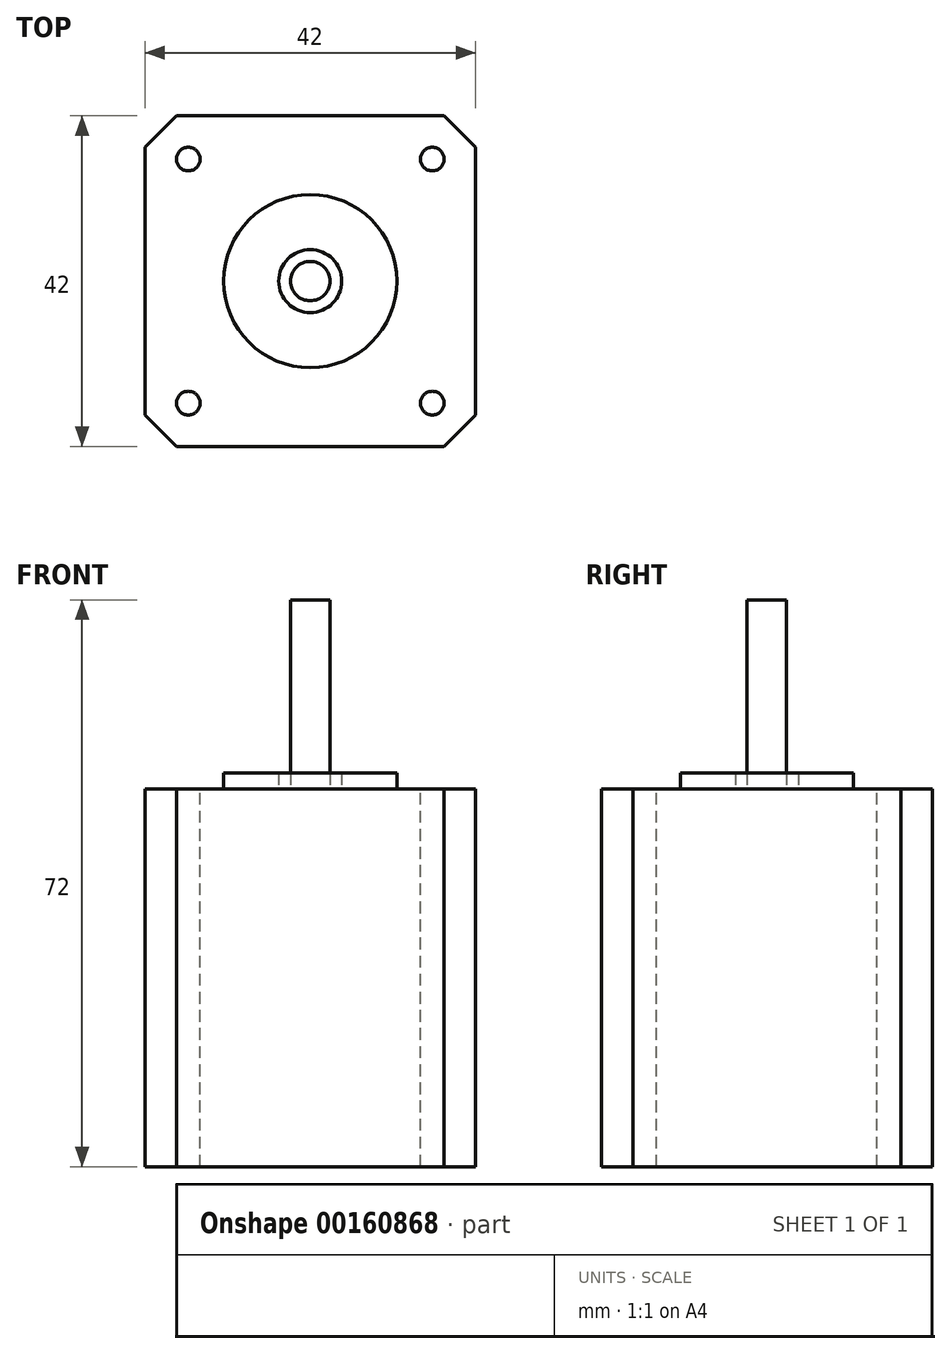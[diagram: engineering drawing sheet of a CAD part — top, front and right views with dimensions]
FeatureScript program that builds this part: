
annotation { "Feature Type Name" : "Feature", "Feature Type Description" : "" }
export const myFeature = defineFeature(function(context is Context, id is Id, definition is map)
    precondition{}
    {
        {
            var Q0;
            Q0=qCreatedBy(makeId("Top.planeOp"),FACE);
            var sketch = newSketch(context, id + "F0", { "sketchPlane" : qUnion([Q0])});
            skLineSegment(sketch, "E0", {"start": v(-21, 0) * mm, "end": v(-21, 17) * mm});
            skLineSegment(sketch, "E1", {"start": v(-21, 17) * mm, "end": v(-17, 21) * mm});
            skLineSegment(sketch, "E2", {"start": v(-17, 21) * mm, "end": v(0, 21) * mm});
            skLineSegment(sketch, "E3.MirrorCS", {"start": v(17, 21) * mm, "end": v(0, 21) * mm});
            skLineSegment(sketch, "E4.MirrorCS", {"start": v(21, 17) * mm, "end": v(17, 21) * mm});
            skLineSegment(sketch, "E5.MirrorCS", {"start": v(21, 0) * mm, "end": v(21, 17) * mm});
            skLineSegment(sketch, "E6.MirrorCS", {"start": v(21, 0) * mm, "end": v(21, -17) * mm});
            skLineSegment(sketch, "E7.MirrorCS", {"start": v(21, -17) * mm, "end": v(17, -21) * mm});
            skLineSegment(sketch, "E8.MirrorCS", {"start": v(17, -21) * mm, "end": v(0, -21) * mm});
            skLineSegment(sketch, "E9.MirrorCS", {"start": v(-17, -21) * mm, "end": v(0, -21) * mm});
            skLineSegment(sketch, "E10.MirrorCS", {"start": v(-21, -17) * mm, "end": v(-17, -21) * mm});
            skLineSegment(sketch, "E11.MirrorCS", {"start": v(-21, 0) * mm, "end": v(-21, -17) * mm});
            skCircle(sketch, "E12", {"center": v(15.5, 15.5) * mm, "radius": 1.5 * mm});
            skCircle(sketch, "E13.MirrorC", {"center": v(-15.5, 15.5) * mm, "radius": 1.5 * mm});
            skCircle(sketch, "E14.MirrorC", {"center": v(15.5, -15.5) * mm, "radius": 1.5 * mm});
            skCircle(sketch, "E15.MirrorC", {"center": v(-15.5, -15.5) * mm, "radius": 1.5 * mm});
            skSolve(sketch);
        }
        {
            var Q0;
            Q0 = qSketchRegion(id + "F0", true);
            extrude(context, id + "F1", {"entities" : qUnion([Q0]), "oppositeDirection" : true, "depth" : 48 * mm});
        }
        {
            var Q0;
            Q0=makeQuery(id+"F1.opExtrude","CAP_FACE",FACE,{"disambiguationData":[OSD([sQuery(id+"F0.wireOp",EDGE,"E0"),sQuery(id+"F0.wireOp",EDGE,"E1"),sQuery(id+"F0.wireOp",EDGE,"E2"),sQuery(id+"F0.wireOp",EDGE,"E3.MirrorCS"),sQuery(id+"F0.wireOp",EDGE,"E4.MirrorCS"),sQuery(id+"F0.wireOp",EDGE,"E5.MirrorCS"),sQuery(id+"F0.wireOp",EDGE,"E6.MirrorCS"),sQuery(id+"F0.wireOp",EDGE,"E7.MirrorCS"),sQuery(id+"F0.wireOp",EDGE,"E8.MirrorCS"),sQuery(id+"F0.wireOp",EDGE,"E9.MirrorCS"),sQuery(id+"F0.wireOp",EDGE,"E10.MirrorCS"),sQuery(id+"F0.wireOp",EDGE,"E11.MirrorCS"),sQuery(id+"F0.wireOp",EDGE,"E12"),sQuery(id+"F0.wireOp",EDGE,"E13.MirrorC"),sQuery(id+"F0.wireOp",EDGE,"E14.MirrorC"),sQuery(id+"F0.wireOp",EDGE,"E15.MirrorC")])],"isStart":true});
            var sketch = newSketch(context, id + "F2", { "sketchPlane" : qUnion([Q0])});
            skCircle(sketch, "E16", {"center": v(0, 0) * mm, "radius": 11 * mm});
            skCircle(sketch, "E17", {"center": v(0, 0) * mm, "radius": 4 * mm});
            skSolve(sketch);
        }
        {
            var Q0;
            Q0 = qSketchRegion(id + "F2", true);
            extrude(context, id + "F3", {"entities" : qUnion([Q0]), "operationType" : NewBodyOperationType.ADD, "depth" : 2 * mm});
        }
        {
            var Q0;
            {var subQ0=sQuery(id+"F0.wireOp",EDGE,"E13.MirrorC");var subQ1=sQuery(id+"F0.wireOp",EDGE,"E10.MirrorCS");var subQ2=sQuery(id+"F0.wireOp",EDGE,"E9.MirrorCS");var subQ3=sQuery(id+"F0.wireOp",EDGE,"E8.MirrorCS");var subQ4=sQuery(id+"F0.wireOp",EDGE,"E7.MirrorCS");var subQ5=sQuery(id+"F0.wireOp",EDGE,"E6.MirrorCS");var subQ6=sQuery(id+"F0.wireOp",EDGE,"E5.MirrorCS");var subQ7=sQuery(id+"F0.wireOp",EDGE,"E11.MirrorCS");var subQ8=sQuery(id+"F0.wireOp",EDGE,"E0");var subQ9=sQuery(id+"F0.wireOp",EDGE,"E15.MirrorC");var subQ10=sQuery(id+"F0.wireOp",EDGE,"E12");var subQ11=sQuery(id+"F0.wireOp",EDGE,"E1");var subQ12=sQuery(id+"F0.wireOp",EDGE,"E3.MirrorCS");var subQ13=sQuery(id+"F0.wireOp",EDGE,"E2");var subQ14=sQuery(id+"F0.wireOp",EDGE,"E4.MirrorCS");var subQ15=sQuery(id+"F0.wireOp",EDGE,"E14.MirrorC");Q0=makeQuery(id+"F3.boolean.opBoolean","SPLIT",FACE,{"disambiguationData":[TD([makeQuery(id+"F1.opExtrude","SWEPT_FACE",FACE,{"disambiguationData":[OSD([subQ11])]})])],"derivedFrom":makeQuery(id+"F1.opExtrude","CAP_FACE",FACE,{"disambiguationData":[OSD([subQ8,subQ11,subQ13,subQ12,subQ14,subQ6,subQ5,subQ4,subQ3,subQ2,subQ1,subQ7,subQ10,subQ0,subQ15,subQ9])],"isStart":true})});}
            var sketch = newSketch(context, id + "F4", { "sketchPlane" : qUnion([Q0])});
            skCircle(sketch, "E18", {"center": v(0, 0) * mm, "radius": 2.5 * mm});
            skSolve(sketch);
        }
        {
            var Q0;
            Q0 = qSketchRegion(id + "F4", true);
            extrude(context, id + "F5", {"entities" : qUnion([Q0]), "operationType" : NewBodyOperationType.ADD, "depth" : 24 * mm});
        }
    });
